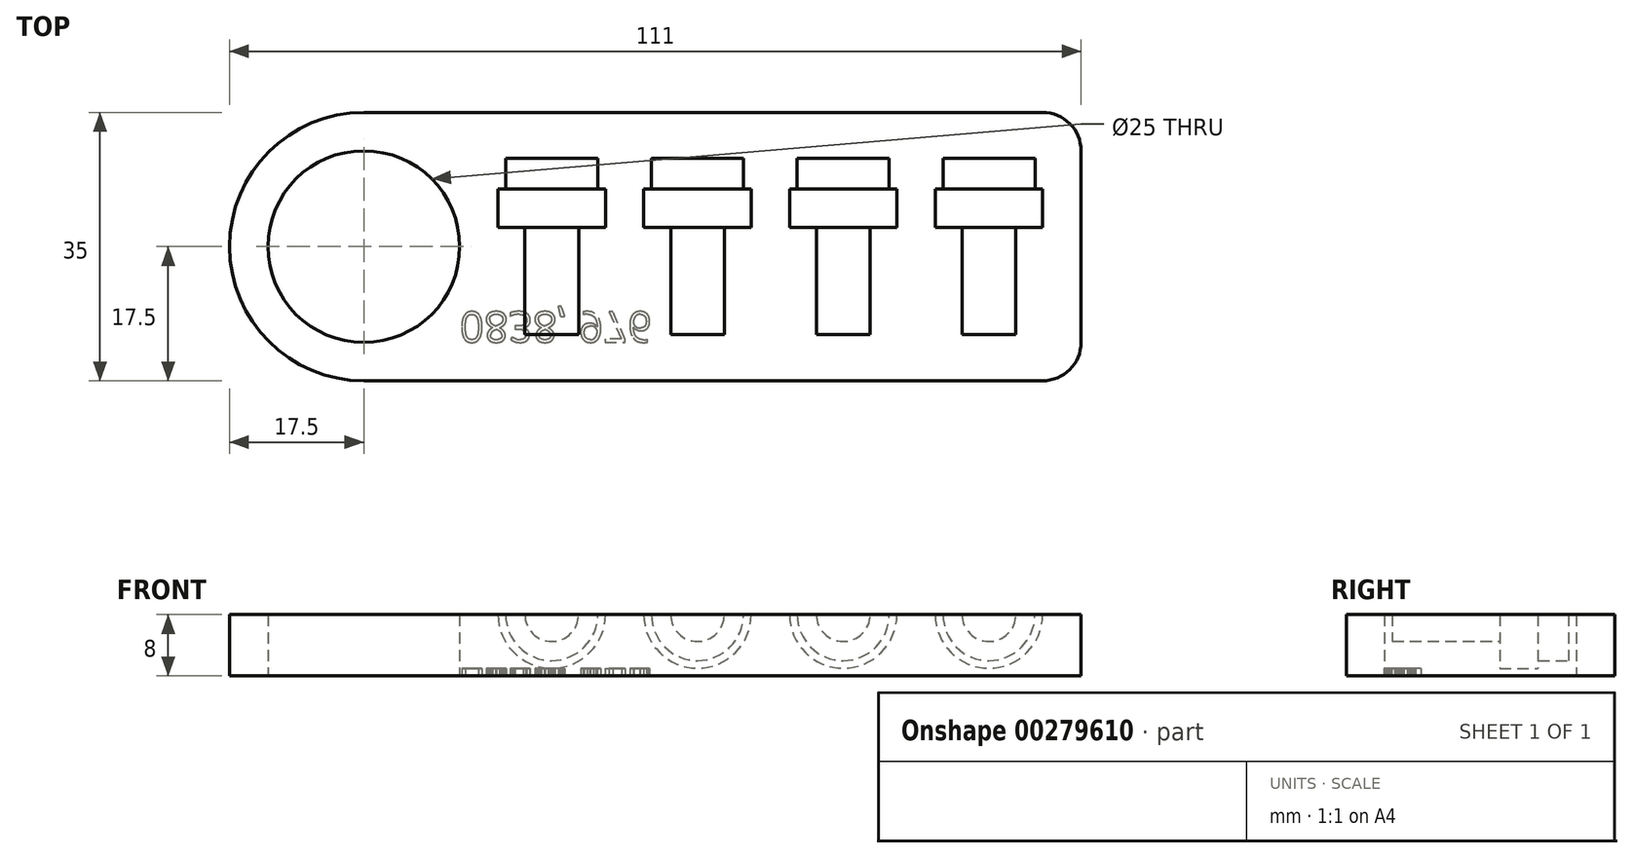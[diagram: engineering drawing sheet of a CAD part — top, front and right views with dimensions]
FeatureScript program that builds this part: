
annotation { "Feature Type Name" : "Feature", "Feature Type Description" : "" }
export const myFeature = defineFeature(function(context is Context, id is Id, definition is map)
    precondition{}
    {
        {
            var Q0;
            Q0=qCreatedBy(makeId("Top.planeOp"),FACE);
            var sketch = newSketch(context, id + "F0", { "sketchPlane" : qUnion([Q0])});
            skLineSegment(sketch, "E0.bottom", {"start": v(17.5, 0) * mm, "end": v(106, 0) * mm});
            skLineSegment(sketch, "E0.top", {"start": v(17.5, 35) * mm, "end": v(106, 35) * mm});
            skLineSegment(sketch, "E0.left", {"start": v(0, 17.5) * mm, "end": v(0, 17.5) * mm});
            skLineSegment(sketch, "E0.right", {"start": v(111, 5) * mm, "end": v(111, 30) * mm});
            skLineSegment(sketch, "E1.bottom", {"start": v(0, 0) * mm, "end": v(17.5, 0) * mm, "construction": true});
            skLineSegment(sketch, "E1.top", {"start": v(0, 17.5) * mm, "end": v(17.5, 17.5) * mm, "construction": true});
            skLineSegment(sketch, "E1.left", {"start": v(0, 0) * mm, "end": v(0, 17.5) * mm, "construction": true});
            skLineSegment(sketch, "E1.right", {"start": v(17.5, 0) * mm, "end": v(17.5, 17.5) * mm, "construction": true});
            skCircle(sketch, "E2", {"center": v(17.5, 17.5) * mm, "radius": 12.5 * mm});
            skPoint(sketch, "E3.visualSharp", {"position": v(0, 0) * mm});
            skArc(sketch, "E3.filletArc", {"start": v(0, 17.5) * mm, "mid": v(5.13, 5.13) * mm, "end": v(17.5, 0) * mm});
            skPoint(sketch, "E4.visualSharp", {"position": v(0, 35) * mm});
            skArc(sketch, "E4.filletArc", {"start": v(17.5, 35) * mm, "mid": v(5.13, 29.87) * mm, "end": v(0, 17.5) * mm});
            skPoint(sketch, "E5.visualSharp", {"position": v(111, 35) * mm});
            skArc(sketch, "E5.filletArc", {"start": v(111, 30) * mm, "mid": v(109.54, 33.54) * mm, "end": v(106, 35) * mm});
            skPoint(sketch, "E6.visualSharp", {"position": v(111, 0) * mm});
            skArc(sketch, "E6.filletArc", {"start": v(106, 0) * mm, "mid": v(109.54, 1.46) * mm, "end": v(111, 5) * mm});
            skSolve(sketch);
        }
        {
            var Q0;
            Q0=makeQuery(id+"F0.imprint","IMPRINT",FACE,{"disambiguationData":[TD([[makeQuery(id+"F0.imprint","IMPRINT",EDGE,{"derivedFrom":sQuery(id+"F0.wireOp",EDGE,"E0.bottom")}),1.0]])]});
            extrude(context, id + "F1", {"entities" : qUnion([Q0]), "depth" : 8 * mm});
        }
        {
            var Q0;
            Q0=makeQuery(id+"F1.opExtrude","CAP_FACE",FACE,{"disambiguationData":[OSD([sQuery(id+"F0.wireOp",EDGE,"E0.bottom"),sQuery(id+"F0.wireOp",EDGE,"E0.top"),sQuery(id+"F0.wireOp",EDGE,"E0.right"),sQuery(id+"F0.wireOp",EDGE,"E2"),sQuery(id+"F0.wireOp",EDGE,"E3.filletArc"),sQuery(id+"F0.wireOp",EDGE,"E4.filletArc"),sQuery(id+"F0.wireOp",EDGE,"E5.filletArc"),sQuery(id+"F0.wireOp",EDGE,"E6.filletArc")])],"isStart":false});
            var sketch = newSketch(context, id + "F2", { "sketchPlane" : qUnion([Q0])});
            skLineSegment(sketch, "E7.bottom", {"start": v(0, 0) * mm, "end": v(42, 0) * mm, "construction": true});
            skLineSegment(sketch, "E7.top", {"start": v(0, 6) * mm, "end": v(42, 6) * mm, "construction": true});
            skLineSegment(sketch, "E7.left", {"start": v(0, 0) * mm, "end": v(0, 6) * mm, "construction": true});
            skLineSegment(sketch, "E7.right", {"start": v(42, 0) * mm, "end": v(42, 6) * mm, "construction": true});
            skLineSegment(sketch, "E8", {"start": v(42, 6) * mm, "end": v(61, 6) * mm, "construction": true});
            skLineSegment(sketch, "E9", {"start": v(61, 6) * mm, "end": v(80, 6) * mm, "construction": true});
            skLineSegment(sketch, "E10", {"start": v(80, 6) * mm, "end": v(99, 6) * mm, "construction": true});
            skLineSegment(sketch, "E11.bottom", {"start": v(42, 6) * mm, "end": v(45.5, 6) * mm});
            skLineSegment(sketch, "E11.left", {"start": v(42, 6) * mm, "end": v(42, 20) * mm});
            skLineSegment(sketch, "E11.right", {"start": v(45.5, 6) * mm, "end": v(45.5, 20) * mm});
            skLineSegment(sketch, "E12.bottom", {"start": v(45.5, 20) * mm, "end": v(49, 20) * mm});
            skLineSegment(sketch, "E12.top", {"start": v(48, 25) * mm, "end": v(49, 25) * mm});
            skLineSegment(sketch, "E12.left", {"start": v(42, 20) * mm, "end": v(42, 25) * mm});
            skLineSegment(sketch, "E12.right", {"start": v(49, 20) * mm, "end": v(49, 25) * mm});
            skLineSegment(sketch, "E13.top", {"start": v(42, 29) * mm, "end": v(48, 29) * mm});
            skLineSegment(sketch, "E13.left", {"start": v(42, 25) * mm, "end": v(42, 29) * mm});
            skLineSegment(sketch, "E13.right", {"start": v(48, 25) * mm, "end": v(48, 29) * mm});
            skLineSegment(sketch, "E14.bottom", {"start": v(61, 6) * mm, "end": v(64.5, 6) * mm});
            skLineSegment(sketch, "E14.left", {"start": v(61, 6) * mm, "end": v(61, 20) * mm});
            skLineSegment(sketch, "E14.right", {"start": v(64.5, 6) * mm, "end": v(64.5, 20) * mm});
            skLineSegment(sketch, "E15.bottom", {"start": v(64.5, 20) * mm, "end": v(68, 20) * mm});
            skLineSegment(sketch, "E15.top", {"start": v(67, 25) * mm, "end": v(68, 25) * mm});
            skLineSegment(sketch, "E15.left", {"start": v(61, 20) * mm, "end": v(61, 25) * mm});
            skLineSegment(sketch, "E15.right", {"start": v(68, 20) * mm, "end": v(68, 25) * mm});
            skLineSegment(sketch, "E16.top", {"start": v(61, 29) * mm, "end": v(67, 29) * mm});
            skLineSegment(sketch, "E16.left", {"start": v(61, 25) * mm, "end": v(61, 29) * mm});
            skLineSegment(sketch, "E16.right", {"start": v(67, 25) * mm, "end": v(67, 29) * mm});
            skLineSegment(sketch, "E17.bottom", {"start": v(80, 6) * mm, "end": v(83.5, 6) * mm});
            skLineSegment(sketch, "E17.left", {"start": v(80, 6) * mm, "end": v(80, 20) * mm});
            skLineSegment(sketch, "E17.right", {"start": v(83.5, 6) * mm, "end": v(83.5, 20) * mm});
            skLineSegment(sketch, "E18.bottom", {"start": v(83.5, 20) * mm, "end": v(87, 20) * mm});
            skLineSegment(sketch, "E18.top", {"start": v(86, 25) * mm, "end": v(87, 25) * mm});
            skLineSegment(sketch, "E18.left", {"start": v(80, 20) * mm, "end": v(80, 25) * mm});
            skLineSegment(sketch, "E18.right", {"start": v(87, 20) * mm, "end": v(87, 25) * mm});
            skLineSegment(sketch, "E19.top", {"start": v(80, 29) * mm, "end": v(86, 29) * mm});
            skLineSegment(sketch, "E19.left", {"start": v(80, 25) * mm, "end": v(80, 29) * mm});
            skLineSegment(sketch, "E19.right", {"start": v(86, 25) * mm, "end": v(86, 29) * mm});
            skLineSegment(sketch, "E20.bottom", {"start": v(99, 6) * mm, "end": v(102.5, 6) * mm});
            skLineSegment(sketch, "E20.left", {"start": v(99, 6) * mm, "end": v(99, 20) * mm});
            skLineSegment(sketch, "E20.right", {"start": v(102.5, 6) * mm, "end": v(102.5, 20) * mm});
            skLineSegment(sketch, "E21.bottom", {"start": v(102.5, 20) * mm, "end": v(106, 20) * mm});
            skLineSegment(sketch, "E21.top", {"start": v(105, 25) * mm, "end": v(106, 25) * mm});
            skLineSegment(sketch, "E21.left", {"start": v(99, 20) * mm, "end": v(99, 25) * mm});
            skLineSegment(sketch, "E21.right", {"start": v(106, 20) * mm, "end": v(106, 25) * mm});
            skLineSegment(sketch, "E22.top", {"start": v(99, 29) * mm, "end": v(105, 29) * mm});
            skLineSegment(sketch, "E22.left", {"start": v(99, 25) * mm, "end": v(99, 29) * mm});
            skLineSegment(sketch, "E22.right", {"start": v(105, 25) * mm, "end": v(105, 29) * mm});
            skSolve(sketch);
        }
        {
            var Q0;
            Q0=makeQuery(id+"F2.imprint","IMPRINT",FACE,{"disambiguationData":[TD([[makeQuery(id+"F2.imprint","IMPRINT",EDGE,{"derivedFrom":sQuery(id+"F2.wireOp",EDGE,"E11.bottom")}),1.0]])]});
            var Q1;
            Q1=sQuery(id+"F2.wireOp",EDGE,"E12.left");
            revolve(context, id + "F3", {"operationType" : NewBodyOperationType.REMOVE, "entities" : qUnion([Q0]), "axis" : qUnion([Q1]), "revolveType" : RevolveType.FULL, "oppositeDirection" : true});
        }
        {
            var Q0;
            Q0=makeQuery(id+"F2.imprint","IMPRINT",FACE,{"disambiguationData":[TD([[makeQuery(id+"F2.imprint","IMPRINT",EDGE,{"derivedFrom":sQuery(id+"F2.wireOp",EDGE,"E14.bottom")}),1.0]])]});
            var Q1;
            Q1=sQuery(id+"F2.wireOp",EDGE,"E15.left");
            revolve(context, id + "F4", {"operationType" : NewBodyOperationType.REMOVE, "entities" : qUnion([Q0]), "axis" : qUnion([Q1]), "revolveType" : RevolveType.FULL, "oppositeDirection" : true});
        }
        {
            var Q0;
            Q0=makeQuery(id+"F2.imprint","IMPRINT",FACE,{"disambiguationData":[TD([[makeQuery(id+"F2.imprint","IMPRINT",EDGE,{"derivedFrom":sQuery(id+"F2.wireOp",EDGE,"E17.bottom")}),1.0]])]});
            var Q1;
            Q1=sQuery(id+"F2.wireOp",EDGE,"E17.left");
            revolve(context, id + "F5", {"operationType" : NewBodyOperationType.REMOVE, "entities" : qUnion([Q0]), "axis" : qUnion([Q1]), "revolveType" : RevolveType.FULL, "oppositeDirection" : true});
        }
        {
            var Q0;
            Q0=makeQuery(id+"F2.imprint","IMPRINT",FACE,{"disambiguationData":[TD([[makeQuery(id+"F2.imprint","IMPRINT",EDGE,{"derivedFrom":sQuery(id+"F2.wireOp",EDGE,"E20.bottom")}),1.0]])]});
            var Q1;
            Q1=sQuery(id+"F2.wireOp",EDGE,"E20.left");
            revolve(context, id + "F6", {"operationType" : NewBodyOperationType.REMOVE, "entities" : qUnion([Q0]), "axis" : qUnion([Q1]), "revolveType" : RevolveType.FULL, "oppositeDirection" : true});
        }
        {
            var Q0;
            Q0=makeQuery(id+"F1.opExtrude","CAP_FACE",FACE,{"disambiguationData":[OSD([sQuery(id+"F0.wireOp",EDGE,"E0.bottom"),sQuery(id+"F0.wireOp",EDGE,"E0.top"),sQuery(id+"F0.wireOp",EDGE,"E0.right"),sQuery(id+"F0.wireOp",EDGE,"E2"),sQuery(id+"F0.wireOp",EDGE,"E3.filletArc"),sQuery(id+"F0.wireOp",EDGE,"E4.filletArc"),sQuery(id+"F0.wireOp",EDGE,"E5.filletArc"),sQuery(id+"F0.wireOp",EDGE,"E6.filletArc")])],"isStart":true});
            var sketch = newSketch(context, id + "F7", { "sketchPlane" : qUnion([Q0])});
            skLineSegment(sketch, "E23.bottom", {"start": v(0, 0) * mm, "end": v(30, 0) * mm, "construction": true});
            skLineSegment(sketch, "E23.top", {"start": v(0, -5) * mm, "end": v(30, -5) * mm, "construction": true});
            skLineSegment(sketch, "E23.left", {"start": v(0, 0) * mm, "end": v(0, -5) * mm, "construction": true});
            skLineSegment(sketch, "E23.right", {"start": v(30, 0) * mm, "end": v(30, -5) * mm, "construction": true});
            skText(sketch, "E24", { "text": "0838, 976", "fontName": "OpenSans-Regular.ttf"});
            const initialGuessF7  = {"E24": [0.03, -0.009, 1, 0, 0.004]};
            skSetInitialGuess(sketch, initialGuessF7);
            skSolve(sketch);
        }
        {
            var Q0;
            Q0 = qSketchRegion(id + "F7", true);
            extrude(context, id + "F8", {"entities" : qUnion([Q0]), "operationType" : NewBodyOperationType.REMOVE, "oppositeDirection" : true, "depth" : 1 * mm});
        }
    });
